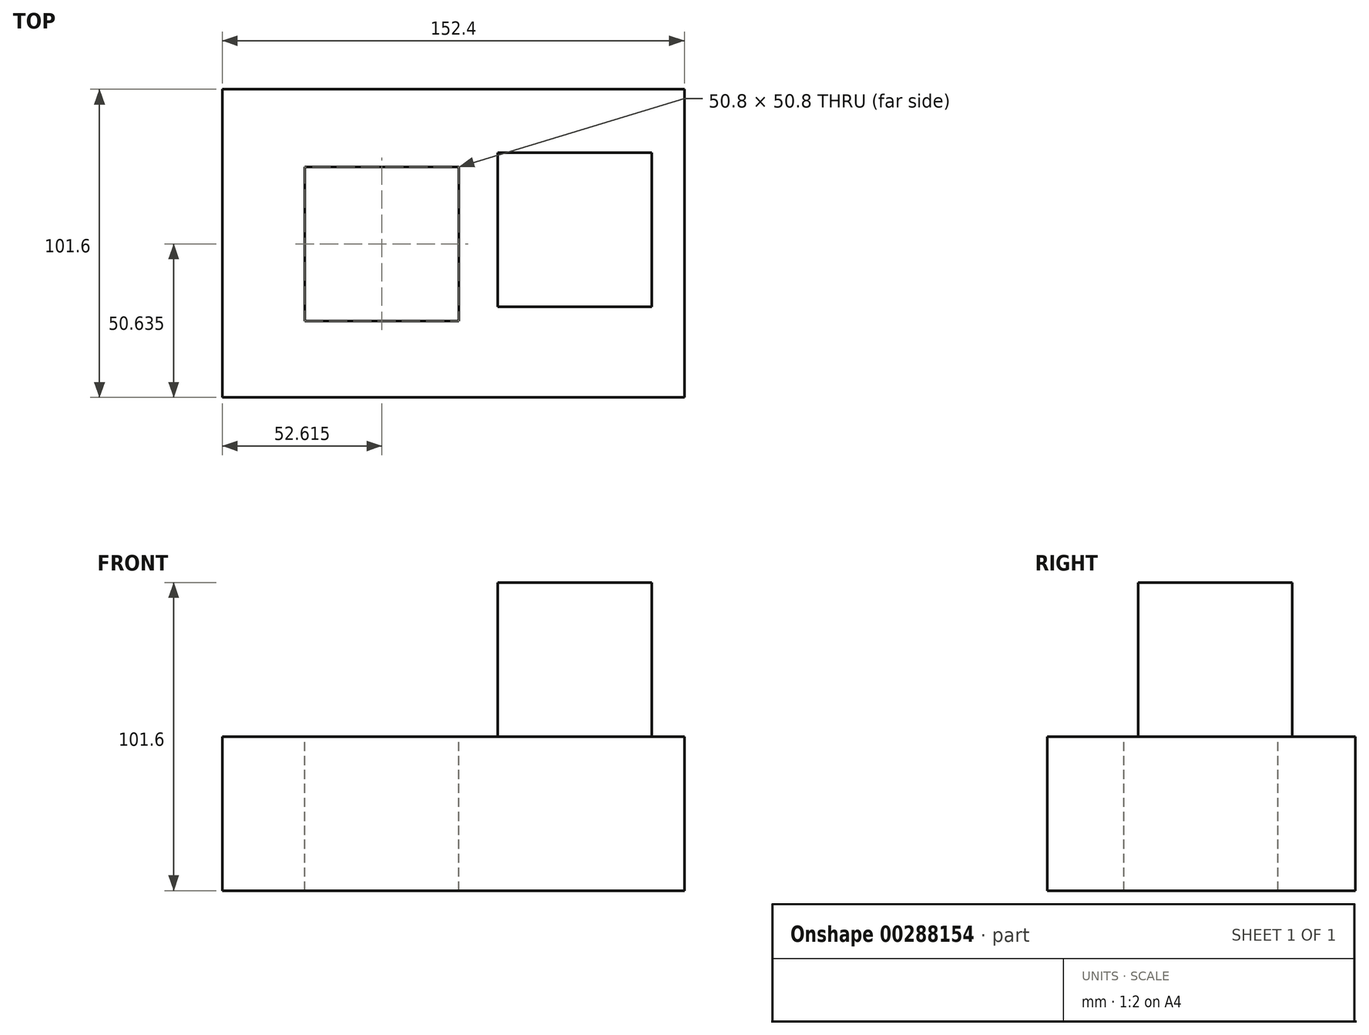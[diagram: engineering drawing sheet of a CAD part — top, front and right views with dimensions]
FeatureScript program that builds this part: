
annotation { "Feature Type Name" : "Feature", "Feature Type Description" : "" }
export const myFeature = defineFeature(function(context is Context, id is Id, definition is map)
    precondition{}
    {
        {
            var Q0;
            Q0=qCreatedBy(makeId("Front.planeOp"),FACE);
            var sketch = newSketch(context, id + "F0", { "sketchPlane" : qUnion([Q0])});
            skLineSegment(sketch, "E0.bottom", {"start": v(0, 0) * mm, "end": v(152.4, 0) * mm});
            skLineSegment(sketch, "E0.top", {"start": v(0, 50.8) * mm, "end": v(152.4, 50.8) * mm});
            skLineSegment(sketch, "E0.left", {"start": v(0, 0) * mm, "end": v(0, 50.8) * mm});
            skLineSegment(sketch, "E0.right", {"start": v(152.4, 0) * mm, "end": v(152.4, 50.8) * mm});
            skSolve(sketch);
        }
        {
            var Q0;
            Q0 = qSketchRegion(id + "F0", true);
            extrude(context, id + "F1", {"entities" : qUnion([Q0]), "depth" : 101.6 * mm});
        }
        {
            var Q0;
            Q0=makeQuery(id+"F1.opExtrude","SWEPT_FACE",FACE,{"disambiguationData":[OSD([sQuery(id+"F0.wireOp",EDGE,"E0.top")])]});
            var sketch = newSketch(context, id + "F2", { "sketchPlane" : qUnion([Q0])});
            skLineSegment(sketch, "E1.bottom", {"start": v(27.21, -25.56) * mm, "end": v(78.01, -25.56) * mm});
            skLineSegment(sketch, "E1.top", {"start": v(27.21, -76.36) * mm, "end": v(78.01, -76.36) * mm});
            skLineSegment(sketch, "E1.left", {"start": v(27.21, -25.56) * mm, "end": v(27.21, -76.36) * mm});
            skLineSegment(sketch, "E1.right", {"start": v(78.01, -25.56) * mm, "end": v(78.01, -76.36) * mm});
            skSolve(sketch);
        }
        {
            var Q0;
            Q0=makeQuery(id+"F2.imprint","IMPRINT",FACE,{"disambiguationData":[TD([[makeQuery(id+"F2.imprint","IMPRINT",EDGE,{"derivedFrom":sQuery(id+"F2.wireOp",EDGE,"E1.bottom")}),-1.0]])]});
            var Q1;
            Q1=makeQuery(id+"F1.opExtrude","SWEPT_FACE",FACE,{"disambiguationData":[OSD([sQuery(id+"F0.wireOp",EDGE,"E0.bottom")])]});
            extrude(context, id + "F3", {"entities" : qUnion([Q0]), "operationType" : NewBodyOperationType.REMOVE, "endBound" : BoundingType.UP_TO_SURFACE, "oppositeDirection" : true, "endBoundEntityFace" : qUnion([Q1]), "depth" : 101.6 * mm});
        }
        {
            var Q0;
            Q0=makeQuery(id+"F1.opExtrude","SWEPT_FACE",FACE,{"disambiguationData":[OSD([sQuery(id+"F0.wireOp",EDGE,"E0.top")])]});
            var sketch = newSketch(context, id + "F4", { "sketchPlane" : qUnion([Q0])});
            skLineSegment(sketch, "E2.bottom", {"start": v(90.86, -71.67) * mm, "end": v(141.66, -71.67) * mm});
            skLineSegment(sketch, "E2.top", {"start": v(90.86, -20.87) * mm, "end": v(141.66, -20.87) * mm});
            skLineSegment(sketch, "E2.left", {"start": v(90.86, -71.67) * mm, "end": v(90.86, -20.87) * mm});
            skLineSegment(sketch, "E2.right", {"start": v(141.66, -71.67) * mm, "end": v(141.66, -20.87) * mm});
            skSolve(sketch);
        }
        {
            var Q0;
            Q0 = qSketchRegion(id + "F4", true);
            extrude(context, id + "F5", {"entities" : qUnion([Q0]), "operationType" : NewBodyOperationType.ADD, "depth" : 50.8 * mm});
        }
    });
